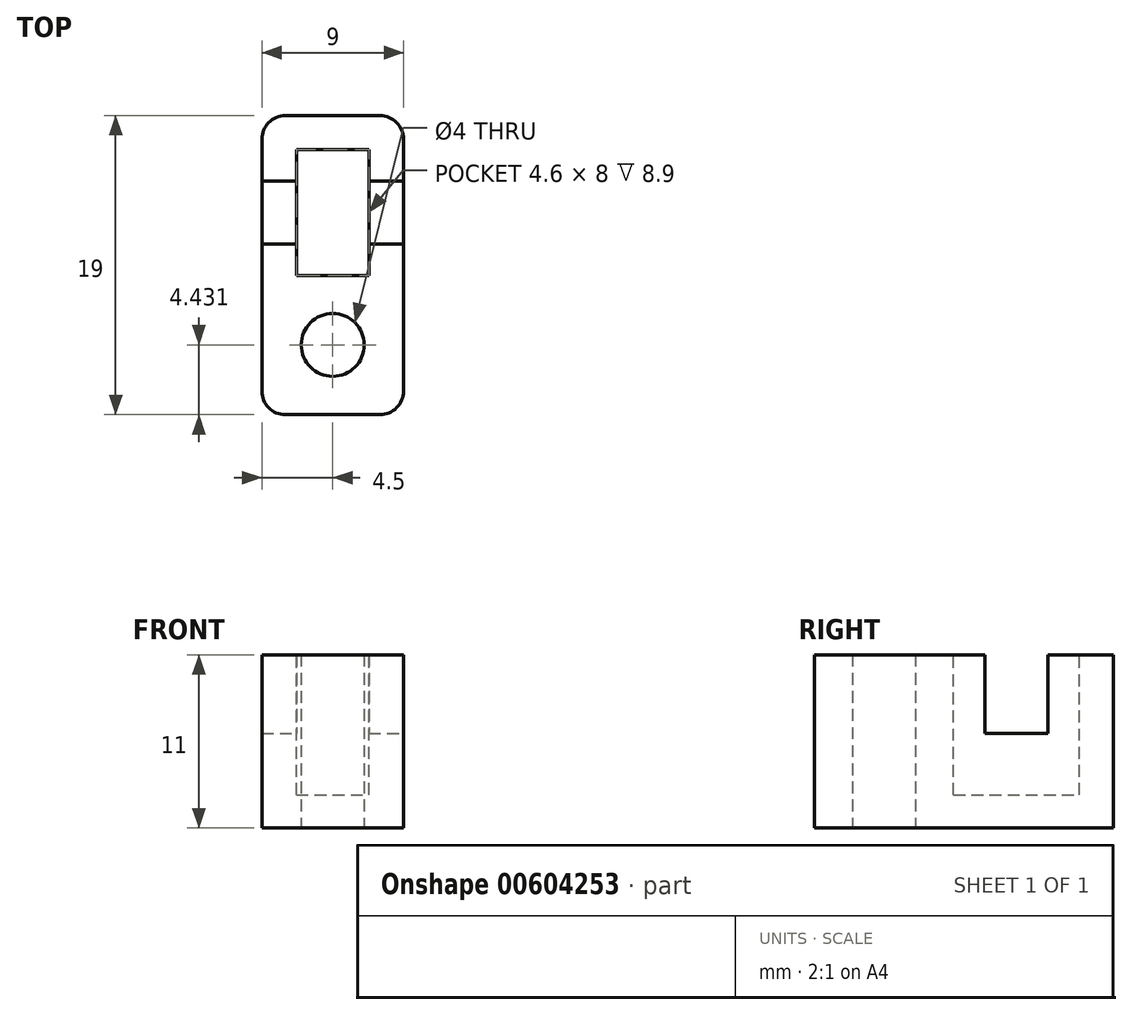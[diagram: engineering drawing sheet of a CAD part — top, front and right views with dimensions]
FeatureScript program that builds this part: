
annotation { "Feature Type Name" : "Feature", "Feature Type Description" : "" }
export const myFeature = defineFeature(function(context is Context, id is Id, definition is map)
    precondition{}
    {
        {
            var Q0;
            Q0=qCreatedBy(makeId("Top.planeOp"),FACE);
            var sketch = newSketch(context, id + "F0", { "sketchPlane" : qUnion([Q0])});
            skLineSegment(sketch, "E0.bottom", {"start": v(-4.5, 9.5) * mm, "end": v(4.5, 9.5) * mm});
            skLineSegment(sketch, "E0.top", {"start": v(-4.5, -9.5) * mm, "end": v(4.5, -9.5) * mm});
            skLineSegment(sketch, "E0.left", {"start": v(-4.5, 9.5) * mm, "end": v(-4.5, -9.5) * mm});
            skLineSegment(sketch, "E0.right", {"start": v(4.5, 9.5) * mm, "end": v(4.5, -9.5) * mm});
            skPoint(sketch, "E1", {"position": v(4.5, 0) * mm});
            skPoint(sketch, "E2", {"position": v(0, -9.5) * mm});
            skSolve(sketch);
        }
        {
            var Q0;
            Q0=makeQuery(id+"F0.imprint","IMPRINT",FACE,{"disambiguationData":[TD([[makeQuery(id+"F0.imprint","IMPRINT",EDGE,{"derivedFrom":sQuery(id+"F0.wireOp",EDGE,"E0.bottom")}),-1.0]])]});
            extrude(context, id + "F1", {"entities" : qUnion([Q0]), "depth" : 11 * mm, "offsetDistance" : 25 * mm});
        }
        {
            var Q0;
            Q0=makeQuery(id+"F1.opExtrude","CAP_FACE",FACE,{"disambiguationData":[OSD([sQuery(id+"F0.wireOp",EDGE,"E0.bottom"),sQuery(id+"F0.wireOp",EDGE,"E0.top"),sQuery(id+"F0.wireOp",EDGE,"E0.left"),sQuery(id+"F0.wireOp",EDGE,"E0.right")])],"isStart":true});
            cPlane(context, id + "F2", {"entities" : qUnion([Q0]), "cplaneType" : CPlaneType.OFFSET, "offset" : 0 * mm, "width" : 150 * mm, "height" : 150 * mm});
        }
        {
            var Q0;
            Q0=qCreatedBy(id+"F2.planeOp",FACE);
            var sketch = newSketch(context, id + "F3", { "sketchPlane" : qUnion([Q0])});
            skCircle(sketch, "E3", {"center": v(0, 5.07) * mm, "radius": 2 * mm});
            skSolve(sketch);
        }
        {
            var Q0;
            Q0=makeQuery(id+"F3.imprint","IMPRINT",FACE,{"disambiguationData":[TD([[makeQuery(id+"F3.imprint","IMPRINT",EDGE,{"derivedFrom":sQuery(id+"F3.wireOp",EDGE,"E3")}),1.0]])]});
            extrude(context, id + "F4", {"entities" : qUnion([Q0]), "operationType" : NewBodyOperationType.REMOVE, "oppositeDirection" : true, "depth" : 11 * mm, "offsetDistance" : 25 * mm});
        }
        {
            var Q0;
            Q0=makeQuery(id+"F1.opExtrude","CAP_FACE",FACE,{"disambiguationData":[OSD([sQuery(id+"F0.wireOp",EDGE,"E0.bottom"),sQuery(id+"F0.wireOp",EDGE,"E0.top"),sQuery(id+"F0.wireOp",EDGE,"E0.left"),sQuery(id+"F0.wireOp",EDGE,"E0.right")])],"isStart":false});
            cPlane(context, id + "F5", {"entities" : qUnion([Q0]), "cplaneType" : CPlaneType.OFFSET, "offset" : 0 * mm, "width" : 150 * mm, "height" : 150 * mm});
        }
        {
            var Q0;
            Q0=qCreatedBy(id+"F5.planeOp",FACE);
            var sketch = newSketch(context, id + "F6", { "sketchPlane" : qUnion([Q0])});
            skLineSegment(sketch, "E4.bottom", {"start": v(-4.55, 5.13) * mm, "end": v(4.45, 5.13) * mm});
            skLineSegment(sketch, "E4.top", {"start": v(-4.55, 1.53) * mm, "end": v(4.45, 1.53) * mm});
            skLineSegment(sketch, "E4.left", {"start": v(-4.55, 5.13) * mm, "end": v(-4.55, 1.53) * mm});
            skLineSegment(sketch, "E4.right", {"start": v(4.45, 5.13) * mm, "end": v(4.45, 1.53) * mm});
            skPoint(sketch, "E5", {"position": v(-4.55, 3.33) * mm});
            skLineSegment(sketch, "E6.bottom", {"start": v(-2.3, -0.67) * mm, "end": v(2.3, -0.67) * mm});
            skLineSegment(sketch, "E6.top", {"start": v(-2.3, 7.33) * mm, "end": v(2.3, 7.33) * mm});
            skLineSegment(sketch, "E6.left", {"start": v(-2.3, -0.67) * mm, "end": v(-2.3, 7.33) * mm});
            skLineSegment(sketch, "E6.right", {"start": v(2.3, -0.67) * mm, "end": v(2.3, 7.33) * mm});
            skPoint(sketch, "E6.middle", {"position": v(0, 3.33) * mm});
            skSolve(sketch);
        }
        {
            var Q0;
            {var subQ0=sQuery(id+"F6.wireOp",EDGE,"E6.left");var subQ1=sQuery(id+"F6.wireOp",EDGE,"E4.bottom");var subQ2=makeQuery(id+"F6.imprint","INTERSECT",VERTEX,{"derivedFrom":[subQ1,subQ0]});Q0=makeQuery(id+"F6.imprint","IMPRINT",FACE,{"disambiguationData":[TD([[makeQuery(id+"F6.imprint","IMPRINT",EDGE,{"disambiguationData":[TD([[subQ2,-1.0]])],"derivedFrom":subQ1}),-1.0]])]});}
            var Q1;
            {var subQ5=sQuery(id+"F6.wireOp",EDGE,"E6.top");Q1=makeQuery(id+"F6.imprint","IMPRINT",FACE,{"disambiguationData":[TD([[makeQuery(id+"F6.imprint","IMPRINT",EDGE,{"derivedFrom":subQ5}),-1.0]])]});}
            var Q2;
            {var subQ5=sQuery(id+"F6.wireOp",EDGE,"E6.bottom");Q2=makeQuery(id+"F6.imprint","IMPRINT",FACE,{"disambiguationData":[TD([[makeQuery(id+"F6.imprint","IMPRINT",EDGE,{"derivedFrom":subQ5}),1.0]])]});}
            extrude(context, id + "F7", {"entities" : qUnion([Q0, Q1, Q2]), "operationType" : NewBodyOperationType.REMOVE, "oppositeDirection" : true, "depth" : 8.9 * mm, "offsetDistance" : 25 * mm});
        }
        {
            var Q0;
            Q0=qCreatedBy(id+"F5.planeOp",FACE);
            var sketch = newSketch(context, id + "F8", { "sketchPlane" : qUnion([Q0])});
            skPoint(sketch, "E7", {"position": v(0, 3.33) * mm});
            skLineSegment(sketch, "E8.bottom", {"start": v(-4.5, 1.33) * mm, "end": v(4.5, 1.33) * mm});
            skLineSegment(sketch, "E8.top", {"start": v(-4.5, 5.33) * mm, "end": v(4.5, 5.33) * mm});
            skLineSegment(sketch, "E8.left", {"start": v(-4.5, 1.33) * mm, "end": v(-4.5, 5.33) * mm});
            skLineSegment(sketch, "E8.right", {"start": v(4.5, 1.33) * mm, "end": v(4.5, 5.33) * mm});
            skSolve(sketch);
        }
        {
            var Q0;
            Q0=makeQuery(id+"F8.imprint","IMPRINT",FACE,{"disambiguationData":[TD([[makeQuery(id+"F8.imprint","IMPRINT",EDGE,{"derivedFrom":sQuery(id+"F8.wireOp",EDGE,"E8.bottom")}),1.0]])]});
            extrude(context, id + "F9", {"entities" : qUnion([Q0]), "operationType" : NewBodyOperationType.REMOVE, "oppositeDirection" : true, "depth" : 5 * mm, "offsetDistance" : 25 * mm});
        }
        {
            var Q0;
            Q0=makeQuery(id+"F1.opExtrude","SWEPT_EDGE",EDGE,{"disambiguationData":[OSD([sQuery(id+"F0.wireOp",EDGE,"E0.bottom"),sQuery(id+"F0.wireOp",EDGE,"E0.right")])]});
            var Q1;
            Q1=makeQuery(id+"F1.opExtrude","SWEPT_EDGE",EDGE,{"disambiguationData":[OSD([sQuery(id+"F0.wireOp",EDGE,"E0.bottom"),sQuery(id+"F0.wireOp",EDGE,"E0.left")])]});
            var Q2;
            Q2=makeQuery(id+"F1.opExtrude","SWEPT_EDGE",EDGE,{"disambiguationData":[OSD([sQuery(id+"F0.wireOp",EDGE,"E0.top"),sQuery(id+"F0.wireOp",EDGE,"E0.right")])]});
            var Q3;
            Q3=makeQuery(id+"F1.opExtrude","SWEPT_EDGE",EDGE,{"disambiguationData":[OSD([sQuery(id+"F0.wireOp",EDGE,"E0.top"),sQuery(id+"F0.wireOp",EDGE,"E0.left")])]});
            fillet(context, id + "F10", {"entities" : qUnion([Q0, Q1, Q2, Q3]), "radius" : 1.5 * mm, "tangentPropagation" : true, "allowEdgeOverflow" : false});
        }
    });
